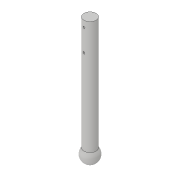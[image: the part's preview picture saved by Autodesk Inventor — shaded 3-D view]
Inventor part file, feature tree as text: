
AUTODESK INVENTOR PART (.ipt)
format: ipt  version: 2019 (Build 230136000, 136)  size: 103,936 bytes
history: native  units: in
note: dims shown in document units (in); Inventor stores cm internally (conversion verified against a paired STEP export)
features: sketch x3, extrude x2, revolve x1
ambient origin geometry x8: Origin, YZ Plane, XZ Plane, XY Plane, X Axis, Y Axis, Z Axis, Center Point
bodies: Solid1 (feature_tree)
feature tree (6):
  revolve  "Revolution1"  Angle=90.0deg
  extrude  "Extrusion1"  Depth=0.0984in
  extrude  "Extrusion2"  Depth=5.5118in TaperAngle=0.0deg
  sketch  "Sketch1"  dims[d2=0.7874in d4=90.0deg]
  sketch  "Sketch2"  dims[d5=5.5118in d6=0.0in d8=0.0984in]
  sketch  "Sketch3"  dims[d9=0.0984in d10=5.5118in d11=0.0in]
